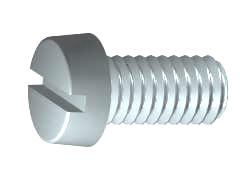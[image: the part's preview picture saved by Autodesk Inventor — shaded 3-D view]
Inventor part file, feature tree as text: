
AUTODESK INVENTOR PART (.ipt)
format: ipt  version: unknown  size: 276,480 bytes
history: native  units: mm (DEFAULTED — no unit token found)
features: other x1, extrude x1, plane x1
ambient origin geometry x7: Origin, YZ Plane, XZ Plane, X Axis, Y Axis, Z Axis, Center Point
feature tree (3):
  other  "Körper"
  extrude  "Loch"  Depth=10.0mm
  plane  "Work Plane1"
